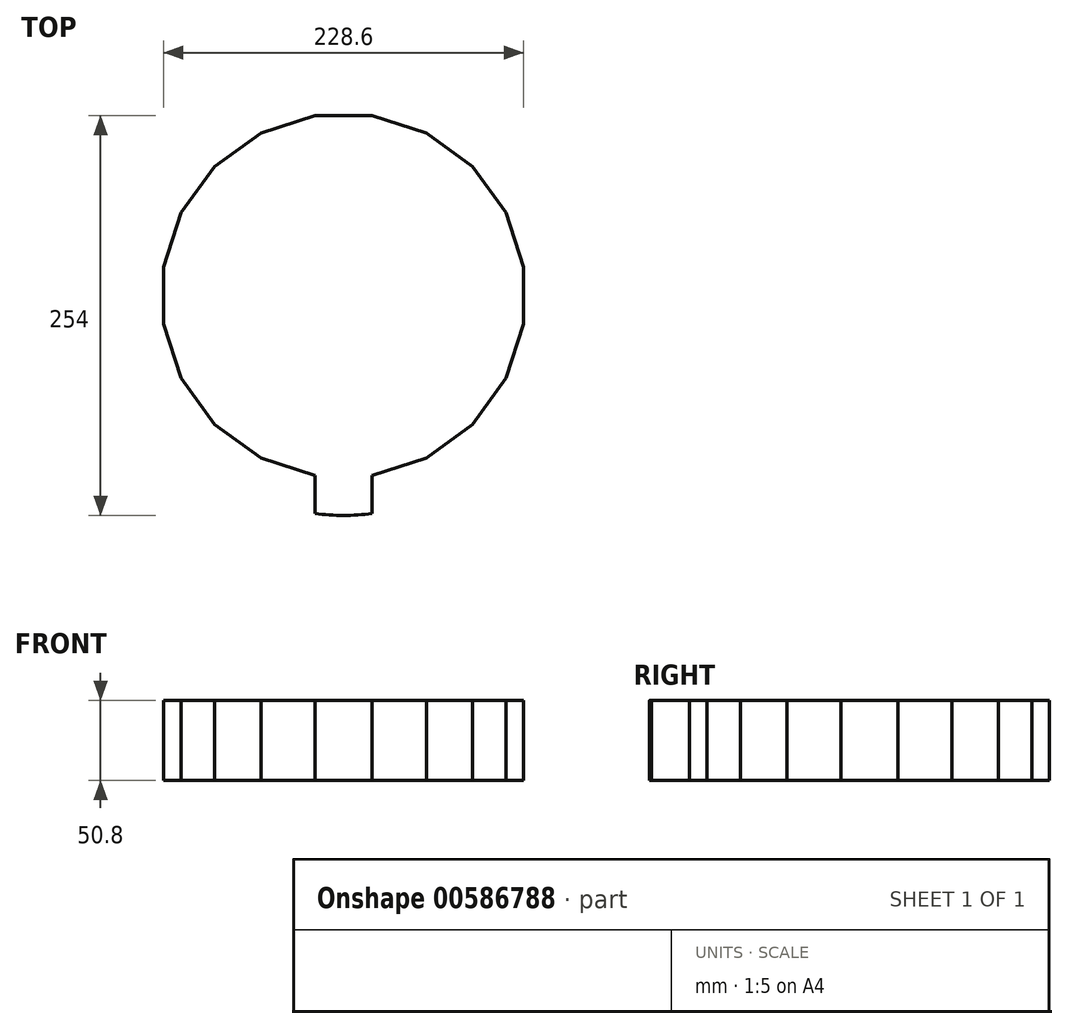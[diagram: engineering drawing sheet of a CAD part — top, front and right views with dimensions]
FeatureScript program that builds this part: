
annotation { "Feature Type Name" : "Feature", "Feature Type Description" : "" }
export const myFeature = defineFeature(function(context is Context, id is Id, definition is map)
    precondition{}
    {
        {
            var Q0;
            Q0=qCreatedBy(makeId("Top.planeOp"),FACE);
            var sketch = newSketch(context, id + "F0", { "sketchPlane" : qUnion([Q0])});
            skCircle(sketch, "E0", {"center": v(0, 0) * mm, "radius": 139.7 * mm});
            skSolve(sketch);
        }
        {
            var Q0;
            Q0 = qSketchRegion(id + "F0", true);
            extrude(context, id + "F1", {"entities" : qUnion([Q0]), "depth" : 50.8 * mm, "offsetDistance" : 25.4 * mm});
        }
        {
            var Q0;
            Q0=makeQuery(id+"F1.opExtrude","CAP_FACE",FACE,{"disambiguationData":[OSD([sQuery(id+"F0.wireOp",EDGE,"E0")])],"isStart":false});
            var sketch = newSketch(context, id + "F2", { "sketchPlane" : qUnion([Q0])});
            skCircle(sketch, "E1.cCircle", {"center": v(0, 0) * mm, "radius": 114.3 * mm, "construction": true});
            skLineSegment(sketch, "E1.0", {"start": v(114.3, 18.1) * mm, "end": v(114.3, -18.1) * mm});
            skLineSegment(sketch, "E1.1", {"start": v(114.3, -18.1) * mm, "end": v(103.11, -52.54) * mm});
            skLineSegment(sketch, "E1.2", {"start": v(103.11, -52.54) * mm, "end": v(81.83, -81.83) * mm});
            skLineSegment(sketch, "E1.3", {"start": v(81.83, -81.83) * mm, "end": v(52.54, -103.11) * mm});
            skLineSegment(sketch, "E1.4", {"start": v(52.54, -103.11) * mm, "end": v(18.1, -114.3) * mm});
            skLineSegment(sketch, "E1.5", {"start": v(18.1, -114.3) * mm, "end": v(-18.1, -114.3) * mm});
            skLineSegment(sketch, "E1.6", {"start": v(-18.1, -114.3) * mm, "end": v(-52.54, -103.11) * mm});
            skLineSegment(sketch, "E1.7", {"start": v(-52.54, -103.11) * mm, "end": v(-81.83, -81.83) * mm});
            skLineSegment(sketch, "E1.8", {"start": v(-81.83, -81.83) * mm, "end": v(-103.11, -52.54) * mm});
            skLineSegment(sketch, "E1.9", {"start": v(-103.11, -52.54) * mm, "end": v(-114.3, -18.1) * mm});
            skLineSegment(sketch, "E1.10", {"start": v(-114.3, -18.1) * mm, "end": v(-114.3, 18.1) * mm});
            skLineSegment(sketch, "E1.11", {"start": v(-114.3, 18.1) * mm, "end": v(-103.11, 52.54) * mm});
            skLineSegment(sketch, "E1.12", {"start": v(-103.11, 52.54) * mm, "end": v(-81.83, 81.83) * mm});
            skLineSegment(sketch, "E1.13", {"start": v(-81.83, 81.83) * mm, "end": v(-52.54, 103.11) * mm});
            skLineSegment(sketch, "E1.14", {"start": v(-52.54, 103.11) * mm, "end": v(-18.1, 114.3) * mm});
            skLineSegment(sketch, "E1.15", {"start": v(-18.1, 114.3) * mm, "end": v(18.1, 114.3) * mm});
            skLineSegment(sketch, "E1.16", {"start": v(18.1, 114.3) * mm, "end": v(52.54, 103.11) * mm});
            skLineSegment(sketch, "E1.17", {"start": v(52.54, 103.11) * mm, "end": v(81.83, 81.83) * mm});
            skLineSegment(sketch, "E1.18", {"start": v(81.83, 81.83) * mm, "end": v(103.11, 52.54) * mm});
            skLineSegment(sketch, "E1.19", {"start": v(103.11, 52.54) * mm, "end": v(114.3, 18.1) * mm});
            skPoint(sketch, "E1.0.midPoint", {"position": v(114.3, 0) * mm});
            skLineSegment(sketch, "E2", {"start": v(0, 114.3) * mm, "end": v(0, 139.7) * mm, "construction": true});
            skCircle(sketch, "E3", {"center": v(0, 0) * mm, "radius": 185.8 * mm, "construction": true});
            skLineSegment(sketch, "E4.top", {"start": v(-18.1, 156.46) * mm, "end": v(18.1, 156.46) * mm});
            skLineSegment(sketch, "E4.left", {"start": v(-18.1, 114.3) * mm, "end": v(-18.1, 156.46) * mm});
            skLineSegment(sketch, "E4.right", {"start": v(18.1, 114.3) * mm, "end": v(18.1, 156.46) * mm});
            skLineSegment(sketch, "E5.1.0", {"start": v(-81.83, 81.83) * mm, "end": v(-106.61, 115.94) * mm});
            skLineSegment(sketch, "E5.1.1", {"start": v(-106.61, 115.94) * mm, "end": v(-77.32, 137.22) * mm});
            skLineSegment(sketch, "E5.1.2", {"start": v(-52.54, 103.11) * mm, "end": v(-77.32, 137.22) * mm});
            skLineSegment(sketch, "E5.2.0", {"start": v(-114.3, 18.1) * mm, "end": v(-154.4, 31.13) * mm});
            skLineSegment(sketch, "E5.2.1", {"start": v(-154.4, 31.13) * mm, "end": v(-143.21, 65.57) * mm});
            skLineSegment(sketch, "E5.2.2", {"start": v(-103.11, 52.54) * mm, "end": v(-143.21, 65.57) * mm});
            skLineSegment(sketch, "E5.3.0", {"start": v(-103.11, -52.54) * mm, "end": v(-143.21, -65.57) * mm});
            skLineSegment(sketch, "E5.3.1", {"start": v(-143.21, -65.57) * mm, "end": v(-154.4, -31.13) * mm});
            skLineSegment(sketch, "E5.3.2", {"start": v(-114.3, -18.1) * mm, "end": v(-154.4, -31.13) * mm});
            skLineSegment(sketch, "E5.4.0", {"start": v(-52.54, -103.11) * mm, "end": v(-77.32, -137.22) * mm});
            skLineSegment(sketch, "E5.4.1", {"start": v(-77.32, -137.22) * mm, "end": v(-106.61, -115.94) * mm});
            skLineSegment(sketch, "E5.4.2", {"start": v(-81.83, -81.83) * mm, "end": v(-106.61, -115.94) * mm});
            skLineSegment(sketch, "E5.5.0", {"start": v(18.1, -114.3) * mm, "end": v(18.1, -156.46) * mm});
            skLineSegment(sketch, "E5.5.1", {"start": v(18.1, -156.46) * mm, "end": v(-18.1, -156.46) * mm});
            skLineSegment(sketch, "E5.5.2", {"start": v(-18.1, -114.3) * mm, "end": v(-18.1, -156.46) * mm});
            skLineSegment(sketch, "E5.6.0", {"start": v(81.83, -81.83) * mm, "end": v(106.61, -115.94) * mm});
            skLineSegment(sketch, "E5.6.1", {"start": v(106.61, -115.94) * mm, "end": v(77.32, -137.22) * mm});
            skLineSegment(sketch, "E5.6.2", {"start": v(52.54, -103.11) * mm, "end": v(77.32, -137.22) * mm});
            skLineSegment(sketch, "E5.7.0", {"start": v(114.3, -18.1) * mm, "end": v(154.4, -31.13) * mm});
            skLineSegment(sketch, "E5.7.1", {"start": v(154.4, -31.13) * mm, "end": v(143.21, -65.57) * mm});
            skLineSegment(sketch, "E5.7.2", {"start": v(103.11, -52.54) * mm, "end": v(143.21, -65.57) * mm});
            skLineSegment(sketch, "E5.8.0", {"start": v(103.11, 52.54) * mm, "end": v(143.21, 65.57) * mm});
            skLineSegment(sketch, "E5.8.1", {"start": v(143.21, 65.57) * mm, "end": v(154.4, 31.13) * mm});
            skLineSegment(sketch, "E5.8.2", {"start": v(114.3, 18.1) * mm, "end": v(154.4, 31.13) * mm});
            skLineSegment(sketch, "E5.9.0", {"start": v(52.54, 103.11) * mm, "end": v(77.32, 137.22) * mm});
            skLineSegment(sketch, "E5.9.1", {"start": v(77.32, 137.22) * mm, "end": v(106.61, 115.94) * mm});
            skLineSegment(sketch, "E5.9.2", {"start": v(81.83, 81.83) * mm, "end": v(106.61, 115.94) * mm});
            skSolve(sketch);
        }
        {
            var Q0;
            {var subQ0=sQuery(id+"F2.wireOp",EDGE,"E1.13");Q0=makeQuery(id+"F2.imprint","IMPRINT",FACE,{"disambiguationData":[TD([[makeQuery(id+"F2.imprint","IMPRINT",EDGE,{"derivedFrom":subQ0}),1.0]])]});}
            var Q1;
            {var subQ0=sQuery(id+"F2.wireOp",EDGE,"E1.15");Q1=makeQuery(id+"F2.imprint","IMPRINT",FACE,{"disambiguationData":[TD([[makeQuery(id+"F2.imprint","IMPRINT",EDGE,{"derivedFrom":subQ0}),1.0]])]});}
            var Q2;
            {var subQ0=sQuery(id+"F2.wireOp",EDGE,"E1.17");Q2=makeQuery(id+"F2.imprint","IMPRINT",FACE,{"disambiguationData":[TD([[makeQuery(id+"F2.imprint","IMPRINT",EDGE,{"derivedFrom":subQ0}),1.0]])]});}
            var Q3;
            {var subQ0=sQuery(id+"F2.wireOp",EDGE,"E1.19");Q3=makeQuery(id+"F2.imprint","IMPRINT",FACE,{"disambiguationData":[TD([[makeQuery(id+"F2.imprint","IMPRINT",EDGE,{"derivedFrom":subQ0}),1.0]])]});}
            var Q4;
            {var subQ0=sQuery(id+"F2.wireOp",EDGE,"E1.1");Q4=makeQuery(id+"F2.imprint","IMPRINT",FACE,{"disambiguationData":[TD([[makeQuery(id+"F2.imprint","IMPRINT",EDGE,{"derivedFrom":subQ0}),1.0]])]});}
            var Q5;
            {var subQ0=sQuery(id+"F2.wireOp",EDGE,"E1.3");Q5=makeQuery(id+"F2.imprint","IMPRINT",FACE,{"disambiguationData":[TD([[makeQuery(id+"F2.imprint","IMPRINT",EDGE,{"derivedFrom":subQ0}),1.0]])]});}
            var Q6;
            {var subQ0=sQuery(id+"F2.wireOp",EDGE,"E1.5");Q6=makeQuery(id+"F2.imprint","IMPRINT",FACE,{"disambiguationData":[TD([[makeQuery(id+"F2.imprint","IMPRINT",EDGE,{"derivedFrom":subQ0}),1.0]])]});}
            var Q7;
            {var subQ0=sQuery(id+"F2.wireOp",EDGE,"E1.7");Q7=makeQuery(id+"F2.imprint","IMPRINT",FACE,{"disambiguationData":[TD([[makeQuery(id+"F2.imprint","IMPRINT",EDGE,{"derivedFrom":subQ0}),1.0]])]});}
            var Q8;
            {var subQ0=sQuery(id+"F2.wireOp",EDGE,"E1.9");Q8=makeQuery(id+"F2.imprint","IMPRINT",FACE,{"disambiguationData":[TD([[makeQuery(id+"F2.imprint","IMPRINT",EDGE,{"derivedFrom":subQ0}),1.0]])]});}
            var Q9;
            {var subQ0=sQuery(id+"F2.wireOp",EDGE,"E1.11");Q9=makeQuery(id+"F2.imprint","IMPRINT",FACE,{"disambiguationData":[TD([[makeQuery(id+"F2.imprint","IMPRINT",EDGE,{"derivedFrom":subQ0}),1.0]])]});}
            var Q10;
            Q10=makeQuery(id+"F2.imprint","IMPRINT",FACE,{"disambiguationData":[TD([[makeQuery(id+"F2.imprint","IMPRINT",EDGE,{"derivedFrom":sQuery(id+"F2.wireOp",EDGE,"E1.0")}),-1.0]])]});
            extrude(context, id + "F3", {"entities" : qUnion([Q0, Q1, Q2, Q3, Q4, Q5, Q6, Q7, Q8, Q9, Q10]), "operationType" : NewBodyOperationType.INTERSECT, "endBound" : BoundingType.THROUGH_ALL, "oppositeDirection" : true, "depth" : 25.4 * mm, "offsetDistance" : 25.4 * mm});
        }
    });
